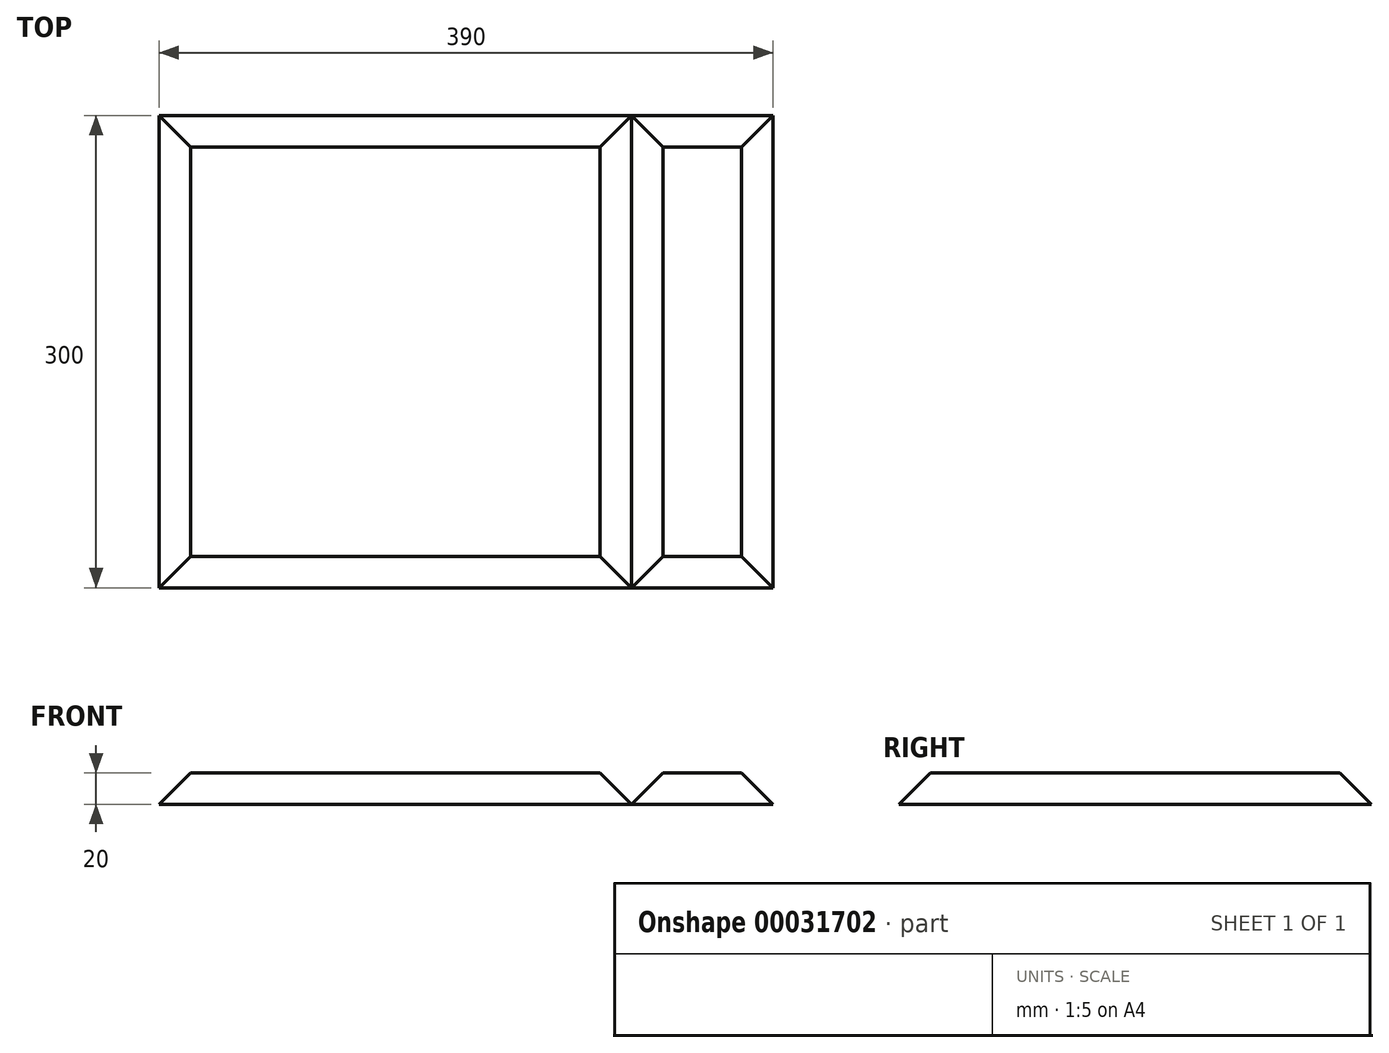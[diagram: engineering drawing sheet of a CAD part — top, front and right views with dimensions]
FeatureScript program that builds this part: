
annotation { "Feature Type Name" : "Feature", "Feature Type Description" : "" }
export const myFeature = defineFeature(function(context is Context, id is Id, definition is map)
    precondition{}
    {
        {
            var Q0;
            Q0=qCreatedBy(makeId("Top.planeOp"),FACE);
            var sketch = newSketch(context, id + "F0", { "sketchPlane" : qUnion([Q0])});
            skLineSegment(sketch, "E0.bottom", {"start": v(0, 0) * mm, "end": v(-300, 0) * mm});
            skLineSegment(sketch, "E0.top", {"start": v(0, 300) * mm, "end": v(-300, 300) * mm});
            skLineSegment(sketch, "E0.left", {"start": v(0, 0) * mm, "end": v(0, 300) * mm});
            skLineSegment(sketch, "E0.right", {"start": v(-300, 0) * mm, "end": v(-300, 300) * mm});
            skSolve(sketch);
        }
        {
            var Q0;
            Q0 = qSketchRegion(id + "F0", true);
            extrude(context, id + "F1", {"entities" : qUnion([Q0]), "depth" : 20 * mm});
        }
        {
            var Q0;
            Q0=makeQuery(id+"F1.opExtrude","CAP_FACE",FACE,{"disambiguationData":[OSD([sQuery(id+"F0.wireOp",EDGE,"E0.bottom"),sQuery(id+"F0.wireOp",EDGE,"E0.top"),sQuery(id+"F0.wireOp",EDGE,"E0.left"),sQuery(id+"F0.wireOp",EDGE,"E0.right")])],"isStart":false});
            chamfer(context, id + "F2", {"entities" : qUnion([Q0]), "width" : 20 * mm, "tangentPropagation" : true});
        }
        {
            var Q0;
            Q0=qCreatedBy(makeId("Top.planeOp"),FACE);
            var sketch = newSketch(context, id + "F3", { "sketchPlane" : qUnion([Q0])});
            skLineSegment(sketch, "E1.bottom", {"start": v(0, 0) * mm, "end": v(90, 0) * mm});
            skLineSegment(sketch, "E1.top", {"start": v(0, 300) * mm, "end": v(90, 300) * mm});
            skLineSegment(sketch, "E1.left", {"start": v(0, 0) * mm, "end": v(0, 300) * mm});
            skLineSegment(sketch, "E1.right", {"start": v(90, 0) * mm, "end": v(90, 300) * mm});
            skSolve(sketch);
        }
        {
            var Q0;
            Q0=makeQuery(id+"F3.imprint","IMPRINT",FACE,{"disambiguationData":[TD([[makeQuery(id+"F3.imprint","IMPRINT",EDGE,{"derivedFrom":sQuery(id+"F3.wireOp",EDGE,"E1.bottom")}),1.0]])]});
            extrude(context, id + "F4", {"entities" : qUnion([Q0]), "depth" : 20 * mm});
        }
        {
            var Q0;
            Q0=makeQuery(id+"F4.opExtrude","CAP_FACE",FACE,{"disambiguationData":[OSD([sQuery(id+"F3.wireOp",EDGE,"E1.bottom"),sQuery(id+"F3.wireOp",EDGE,"E1.top"),sQuery(id+"F3.wireOp",EDGE,"E1.left"),sQuery(id+"F3.wireOp",EDGE,"E1.right")])],"isStart":false});
            chamfer(context, id + "F5", {"entities" : qUnion([Q0]), "width" : 20 * mm, "tangentPropagation" : true});
        }
    });
